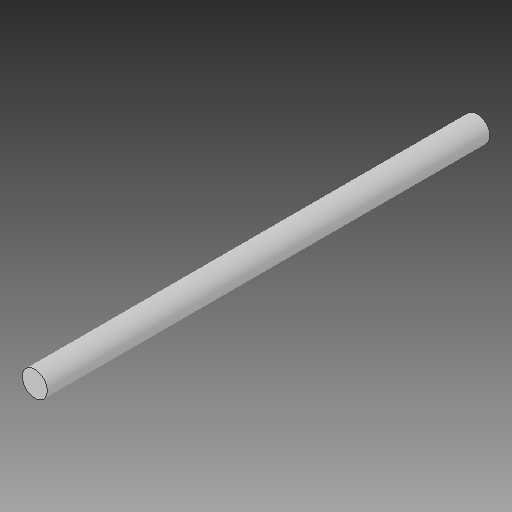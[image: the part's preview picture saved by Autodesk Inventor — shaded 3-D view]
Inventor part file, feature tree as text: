
AUTODESK INVENTOR PART (.ipt)
format: ipt  version: 2017 (Build 210142000, 142)  size: 76,288 bytes
history: native  units: in
note: dims shown in document units (in); Inventor stores cm internally (conversion verified against a paired STEP export)
features: other x3, sketch x1
ambient origin geometry x8: Origin, YZ Plane, XZ Plane, XY Plane, X Axis, Y Axis, Z Axis, Center Point
bodies: Solid1 (feature_tree)
feature tree (4):
  other  "4inax.ipt"
  other  "Solid1::4inax.ipt"
  other  "TaggingFeature1"
  sketch  "Sketch1"  dims[d0=0.3937in]
